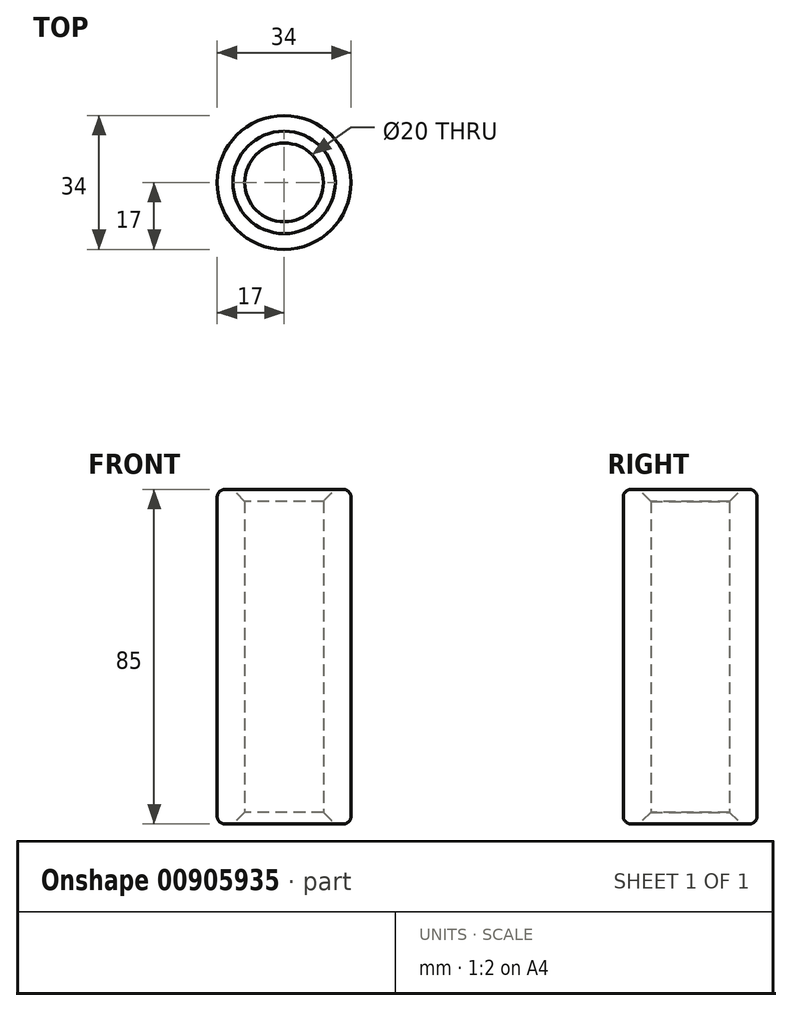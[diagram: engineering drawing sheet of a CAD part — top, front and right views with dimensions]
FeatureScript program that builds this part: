
annotation { "Feature Type Name" : "Feature", "Feature Type Description" : "" }
export const myFeature = defineFeature(function(context is Context, id is Id, definition is map)
    precondition{}
    {
        {
            var Q0;
            Q0=qCreatedBy(makeId("Top.planeOp"),FACE);
            var sketch = newSketch(context, id + "F0", { "sketchPlane" : qUnion([Q0])});
            skCircle(sketch, "E0", {"center": v(0, 0) * mm, "radius": 17 * mm});
            skCircle(sketch, "E1", {"center": v(0, 0) * mm, "radius": 10 * mm});
            skSolve(sketch);
        }
        {
            var Q0;
            Q0 = qSketchRegion(id + "F0", true);
            extrude(context, id + "F1", {"entities" : qUnion([Q0]), "depth" : 85 * mm, "offsetDistance" : 25 * mm});
        }
        {
            var Q0;
            Q0=makeQuery(id+"F1.opExtrude","CAP_EDGE",EDGE,{"disambiguationData":[OSD([sQuery(id+"F0.wireOp",EDGE,"E1")])],"isStart":true});
            var Q1;
            Q1=makeQuery(id+"F1.opExtrude","CAP_EDGE",EDGE,{"disambiguationData":[OSD([sQuery(id+"F0.wireOp",EDGE,"E1")])],"isStart":false});
            chamfer(context, id + "F2", {"entities" : qUnion([Q0, Q1]), "width" : 3 * mm, "tangentPropagation" : true});
        }
        {
            var Q0;
            Q0=makeQuery(id+"F1.opExtrude","CAP_EDGE",EDGE,{"disambiguationData":[OSD([sQuery(id+"F0.wireOp",EDGE,"E0")])],"isStart":false});
            var Q1;
            Q1=makeQuery(id+"F1.opExtrude","CAP_EDGE",EDGE,{"disambiguationData":[OSD([sQuery(id+"F0.wireOp",EDGE,"E0")])],"isStart":true});
            fillet(context, id + "F3", {"entities" : qUnion([Q0, Q1]), "radius" : 2 * mm, "tangentPropagation" : true, "allowEdgeOverflow" : false});
        }
    });
